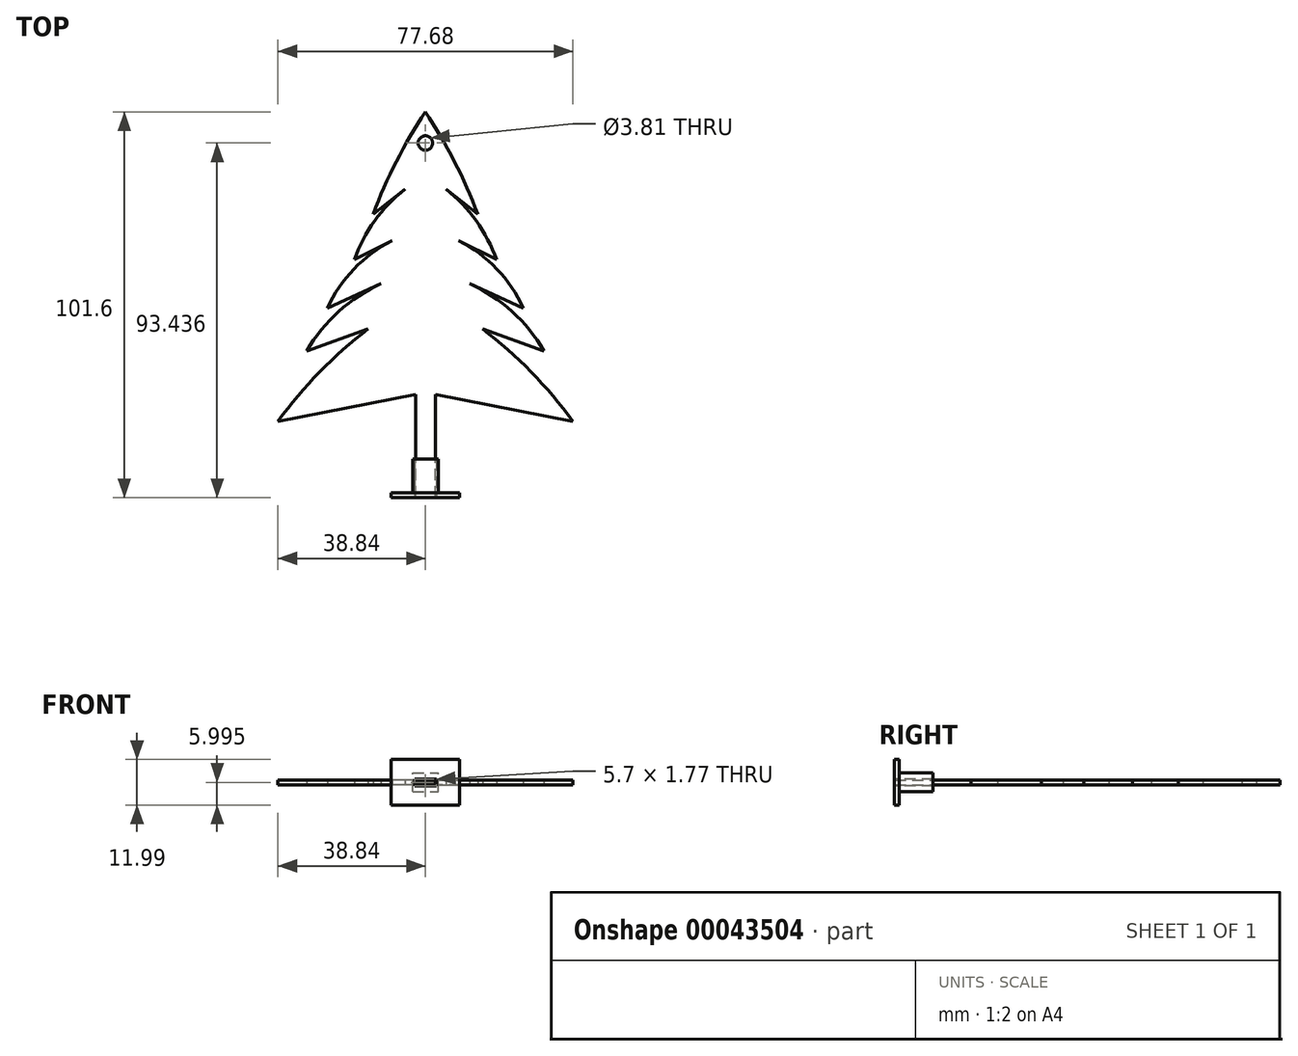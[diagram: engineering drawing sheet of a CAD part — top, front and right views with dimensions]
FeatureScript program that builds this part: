
annotation { "Feature Type Name" : "Feature", "Feature Type Description" : "" }
export const myFeature = defineFeature(function(context is Context, id is Id, definition is map)
    precondition{}
    {
        {
            var Q0;
            Q0=qCreatedBy(makeId("Top.planeOp"),FACE);
            var sketch = newSketch(context, id + "F0", { "sketchPlane" : qUnion([Q0])});
            skLineSegment(sketch, "E0", {"start": v(0, 41.75) * mm, "end": v(0, -59.85) * mm});
            skLineSegment(sketch, "E1", {"start": v(-2.6, -59.85) * mm, "end": v(-2.6, -32.67) * mm});
            skLineSegment(sketch, "E2", {"start": v(-2.6, -32.67) * mm, "end": v(-38.84, -39.73) * mm});
            skLineSegment(sketch, "E3", {"start": v(-15.07, -15.44) * mm, "end": v(-31.27, -21.2) * mm});
            skLineSegment(sketch, "E4", {"start": v(-11.68, -3.43) * mm, "end": v(-25.78, -9.96) * mm});
            skLineSegment(sketch, "E5", {"start": v(-8.8, 7.8) * mm, "end": v(-18.73, 2.84) * mm});
            skLineSegment(sketch, "E6", {"start": v(-5.41, 21.38) * mm, "end": v(-13.77, 14.85) * mm});
            skLineSegment(sketch, "E7", {"start": v(-2.6, -59.85) * mm, "end": v(0, -59.85) * mm});
            skArc(sketch, "E8", {"start": v(0, 41.75) * mm, "mid": v(-7.66, 28.7) * mm, "end": v(-13.77, 14.85) * mm});
            skArc(sketch, "E9", {"start": v(-5.41, 21.38) * mm, "mid": v(-13.4, 13.06) * mm, "end": v(-18.73, 2.84) * mm});
            skArc(sketch, "E10", {"start": v(-8.8, 7.8) * mm, "mid": v(-18.84, 0.4) * mm, "end": v(-25.78, -9.96) * mm});
            skArc(sketch, "E11", {"start": v(-11.68, -3.43) * mm, "mid": v(-22.83, -10.82) * mm, "end": v(-31.27, -21.2) * mm});
            skArc(sketch, "E12", {"start": v(-15.07, -15.44) * mm, "mid": v(-27.85, -26.72) * mm, "end": v(-38.84, -39.73) * mm});
            skLineSegment(sketch, "E13.MirrorCS", {"start": v(2.6, -59.85) * mm, "end": v(0, -59.85) * mm});
            skArc(sketch, "E14.MirrorCS", {"start": v(15.07, -15.44) * mm, "mid": v(27.85, -26.72) * mm, "end": v(38.84, -39.73) * mm});
            skArc(sketch, "E15.MirrorCS", {"start": v(5.41, 21.38) * mm, "mid": v(13.4, 13.06) * mm, "end": v(18.73, 2.84) * mm});
            skArc(sketch, "E16.MirrorCS", {"start": v(11.68, -3.43) * mm, "mid": v(22.83, -10.82) * mm, "end": v(31.27, -21.2) * mm});
            skLineSegment(sketch, "E17.MirrorCS", {"start": v(8.8, 7.8) * mm, "end": v(18.73, 2.84) * mm});
            skArc(sketch, "E18.MirrorCS", {"start": v(0, 41.75) * mm, "mid": v(7.66, 28.7) * mm, "end": v(13.77, 14.85) * mm});
            skLineSegment(sketch, "E19.MirrorCS", {"start": v(2.6, -59.85) * mm, "end": v(2.6, -32.67) * mm});
            skLineSegment(sketch, "E20.MirrorCS", {"start": v(5.41, 21.38) * mm, "end": v(13.77, 14.85) * mm});
            skLineSegment(sketch, "E21.MirrorCS", {"start": v(11.68, -3.43) * mm, "end": v(25.78, -9.96) * mm});
            skLineSegment(sketch, "E22.MirrorCS", {"start": v(15.07, -15.44) * mm, "end": v(31.27, -21.2) * mm});
            skLineSegment(sketch, "E23.MirrorCS", {"start": v(2.6, -32.67) * mm, "end": v(38.84, -39.73) * mm});
            skArc(sketch, "E24.MirrorCS", {"start": v(8.8, 7.8) * mm, "mid": v(18.84, 0.4) * mm, "end": v(25.78, -9.96) * mm});
            skCircle(sketch, "E25", {"center": v(0, 33.59) * mm, "radius": 1.9 * mm});
            skSolve(sketch);
        }
        {
            var Q0;
            Q0 = qSketchRegion(id + "F0", true);
            var Q1;
            Q1=makeQuery(id+"F0.imprint","IMPRINT",FACE,{"disambiguationData":[TD([[makeQuery(id+"F0.imprint","IMPRINT",EDGE,{"derivedFrom":sQuery(id+"F0.wireOp",EDGE,"E1")}),-1.0]])]});
            extrude(context, id + "F1", {"entities" : qUnion([Q0, Q1]), "depth" : 1.27 * mm});
        }
        {
            var Q0;
            Q0=makeQuery(id+"F1.opExtrude","SWEPT_FACE",FACE,{"disambiguationData":[OSD([sQuery(id+"F0.wireOp",EDGE,"E7"),sQuery(id+"F0.wireOp",EDGE,"E13.MirrorCS")])]});
            var sketch = newSketch(context, id + "F2", { "sketchPlane" : qUnion([Q0])});
            skLineSegment(sketch, "E26.rect.bottom", {"start": v(9.02, 6.63) * mm, "end": v(-9.02, 6.63) * mm});
            skLineSegment(sketch, "E26.rect.top", {"start": v(9.02, -5.36) * mm, "end": v(-9.02, -5.36) * mm});
            skLineSegment(sketch, "E26.rect.left", {"start": v(9.02, 6.63) * mm, "end": v(9.02, -5.36) * mm});
            skLineSegment(sketch, "E26.rect.right", {"start": v(-9.02, 6.63) * mm, "end": v(-9.02, -5.36) * mm});
            skPoint(sketch, "E26.rect.middle", {"position": v(0, 0.64) * mm});
            skPoint(sketch, "E26.rect.middle.positionSnap0", {"position": v(2.6, 0.64) * mm});
            skPoint(sketch, "E26.rect.centerSnap0", {"position": v(2.6, 0.64) * mm});
            skLineSegment(sketch, "E27.rect.bottom", {"start": v(-2.6, 1.27) * mm, "end": v(2.6, 1.27) * mm});
            skLineSegment(sketch, "E27.rect.top", {"start": v(-2.6, 0) * mm, "end": v(2.6, 0) * mm});
            skLineSegment(sketch, "E27.rect.left", {"start": v(-2.6, 1.27) * mm, "end": v(-2.6, 0) * mm});
            skLineSegment(sketch, "E27.rect.right", {"start": v(2.6, 1.27) * mm, "end": v(2.6, 0) * mm});
            skLineSegment(sketch, "E28.rect.bottom", {"start": v(3.36, 3.13) * mm, "end": v(-3.36, 3.13) * mm});
            skLineSegment(sketch, "E28.rect.top", {"start": v(3.36, -1.86) * mm, "end": v(-3.36, -1.86) * mm});
            skLineSegment(sketch, "E28.rect.left", {"start": v(3.36, 3.13) * mm, "end": v(3.36, -1.86) * mm});
            skLineSegment(sketch, "E28.rect.right", {"start": v(-3.36, 3.13) * mm, "end": v(-3.36, -1.86) * mm});
            skLineSegment(sketch, "E29.rect.bottom", {"start": v(2.85, -0.25) * mm, "end": v(-2.85, -0.25) * mm});
            skLineSegment(sketch, "E29.rect.top", {"start": v(2.85, 1.52) * mm, "end": v(-2.85, 1.52) * mm});
            skLineSegment(sketch, "E29.rect.left", {"start": v(2.85, -0.25) * mm, "end": v(2.85, 1.52) * mm});
            skLineSegment(sketch, "E29.rect.right", {"start": v(-2.85, -0.25) * mm, "end": v(-2.85, 1.52) * mm});
            skSolve(sketch);
        }
        {
            var Q0;
            Q0=makeQuery(id+"F2.imprint","IMPRINT",FACE,{"disambiguationData":[TD([[makeQuery(id+"F2.imprint","IMPRINT",EDGE,{"derivedFrom":sQuery(id+"F2.wireOp",EDGE,"E28.rect.bottom")}),1.0]])]});
            extrude(context, id + "F3", {"entities" : qUnion([Q0]), "oppositeDirection" : true, "depth" : 10.16 * mm});
        }
        {
            var Q0;
            Q0=makeQuery(id+"F2.imprint","IMPRINT",FACE,{"disambiguationData":[TD([[makeQuery(id+"F2.imprint","IMPRINT",EDGE,{"derivedFrom":sQuery(id+"F2.wireOp",EDGE,"E26.rect.bottom")}),1.0]])]});
            var Q1;
            Q1=makeQuery(id+"F2.imprint","IMPRINT",FACE,{"disambiguationData":[TD([[makeQuery(id+"F2.imprint","IMPRINT",EDGE,{"derivedFrom":sQuery(id+"F2.wireOp",EDGE,"E28.rect.bottom")}),1.0]])]});
            extrude(context, id + "F4", {"entities" : qUnion([Q0, Q1]), "operationType" : NewBodyOperationType.ADD, "oppositeDirection" : true, "depth" : 1.27 * mm});
        }
    });
